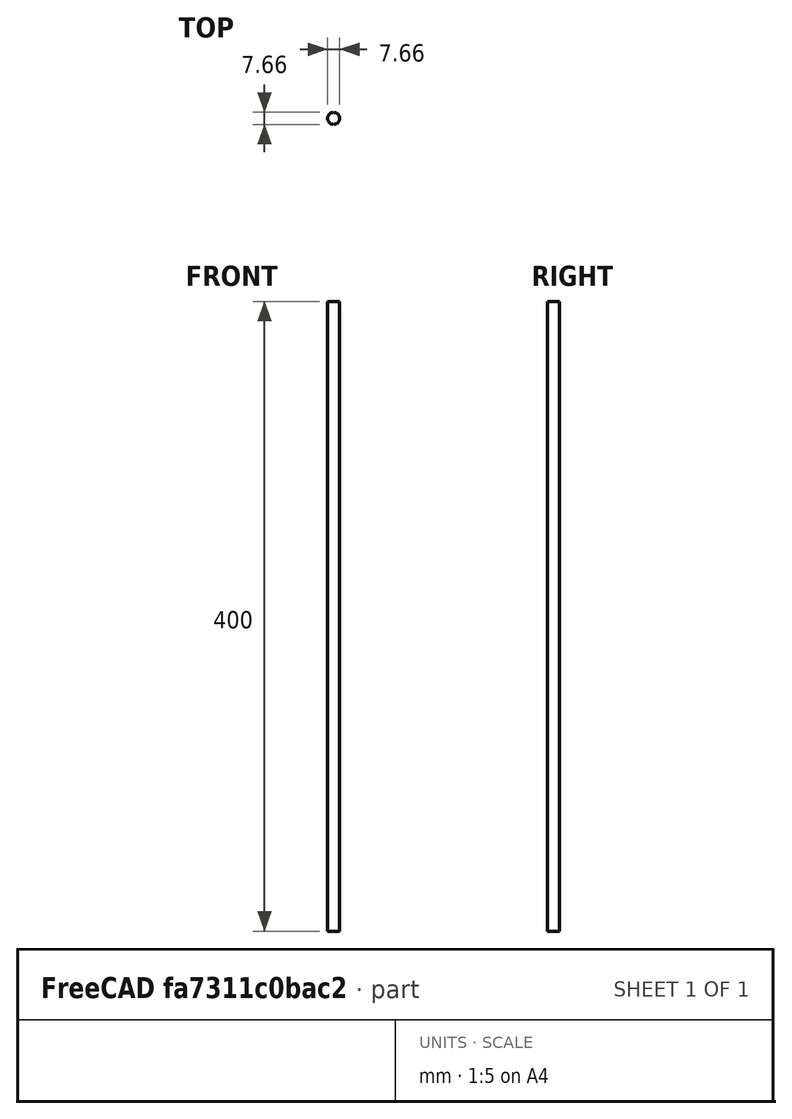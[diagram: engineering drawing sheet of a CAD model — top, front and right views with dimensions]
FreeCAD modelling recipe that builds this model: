
FCSTD DOCUMENT  (FreeCAD 0.18R16093 (Git))
Label: Palo
License: All rights reserved
LicenseURL: http://en.wikipedia.org/wiki/All_rights_reserved
objects: Sketcher::SketchObject×1, PartDesign::Revolution×1, PartDesign::Body×1
note: 4 computed .brp shape members not serialized (recipe doc carries the construction recipe); baked Part::Feature solids carry a one-line shape summary decoded from their .brp

FEATURE [Sketcher::SketchObject] Sketch001
  MapMode = 5
  Placement = pos=(0,0,0) rot=(1,0,0;1.5708rad)
  Support = -> [XZ_Plane003]
  sketch-geometry (4):
    g0: LineSegment StartX=0 StartY=400 StartZ=0 EndX=-3.83 EndY=400 EndZ=0
    g1: LineSegment StartX=-3.83 StartY=400 StartZ=0 EndX=-3.83 EndY=0 EndZ=0
    g2: LineSegment StartX=0 StartY=0 StartZ=0 EndX=0 EndY=400 EndZ=0
    g3: LineSegment StartX=-3.83 StartY=0 StartZ=0 EndX=0 EndY=0 EndZ=0
  constraints (11):
    c: Coincident(g0,g1)
    c: Coincident(g2,g0)
    c: Horizontal(g0)
    c: Vertical(g1)
    c: Vertical(g2)
    c: Distance(g1,g2) = 3.83
    c: DistanceY(g2,g0) = 400
    c: Coincident(g2,g-1)
    c: PointOnObject(g1,g-1)
    c: Coincident(g3,g2)
    c: Coincident(g3,g1)
FEATURE [PartDesign::Revolution] Revolution001
  Angle = 360
  Axis = (0,-2e-16,1)
  Base = (0,0,0)
  Placement = pos=(0,0,0) rot=(1,0,0;1.5708rad)
  Profile = -> Sketch001
  ReferenceAxis = -> Sketch001 [V_Axis]
FEATURE [PartDesign::Body] Body003  label="Palo"
  Group = -> [Sketch001,Revolution001]
  Origin = -> Origin002
  Tip = -> Revolution001
